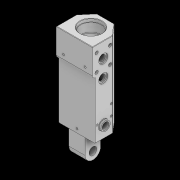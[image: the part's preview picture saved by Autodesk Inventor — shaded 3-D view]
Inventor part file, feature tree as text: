
AUTODESK INVENTOR PART (.ipt)
format: ipt  version: 2021 (Build 250183000, 183)  size: 284,160 bytes
history: native  units: in
note: dims shown in document units (in); Inventor stores cm internally (conversion verified against a paired STEP export)
features: extrude x2, thread x2, sketch x2, projected_geometry x2, other x1
ambient origin geometry x8: Origin, YZ Plane, XZ Plane, XY Plane, X Axis, Y Axis, Z Axis, Center Point
bodies: Solid1 (feature_tree)
feature tree (9):
  extrude  "Extrusion2"  Depth=0.3937in
  extrude  "Extrusion3"  Depth=0.1575in
  thread  "Thread1"  [1 undecoded]
  thread  "Thread2"  [1 undecoded]
  sketch  "Sketch1"  dims[d5=0.3937in d6=0.3937in]
  projected_geometry  "Projected Loop1"
  projected_geometry  "Projected Loop2"
  sketch  "Sketch2"  dims[d7=1.1417in d8=0.0in d9=0.4134in d10=0.4134in d11=0.1969in d12=0.0in d13=0.1575in d14=0.0in d15=0.1575in d16=0.0in]
  other  "M3x0.5 Tapped Hole2"
note: 2 required parameter values undecoded (feature->parameter linkage not recoverable at this tier; creation-order binding heuristic only, values carry confidence <= 0.55)
